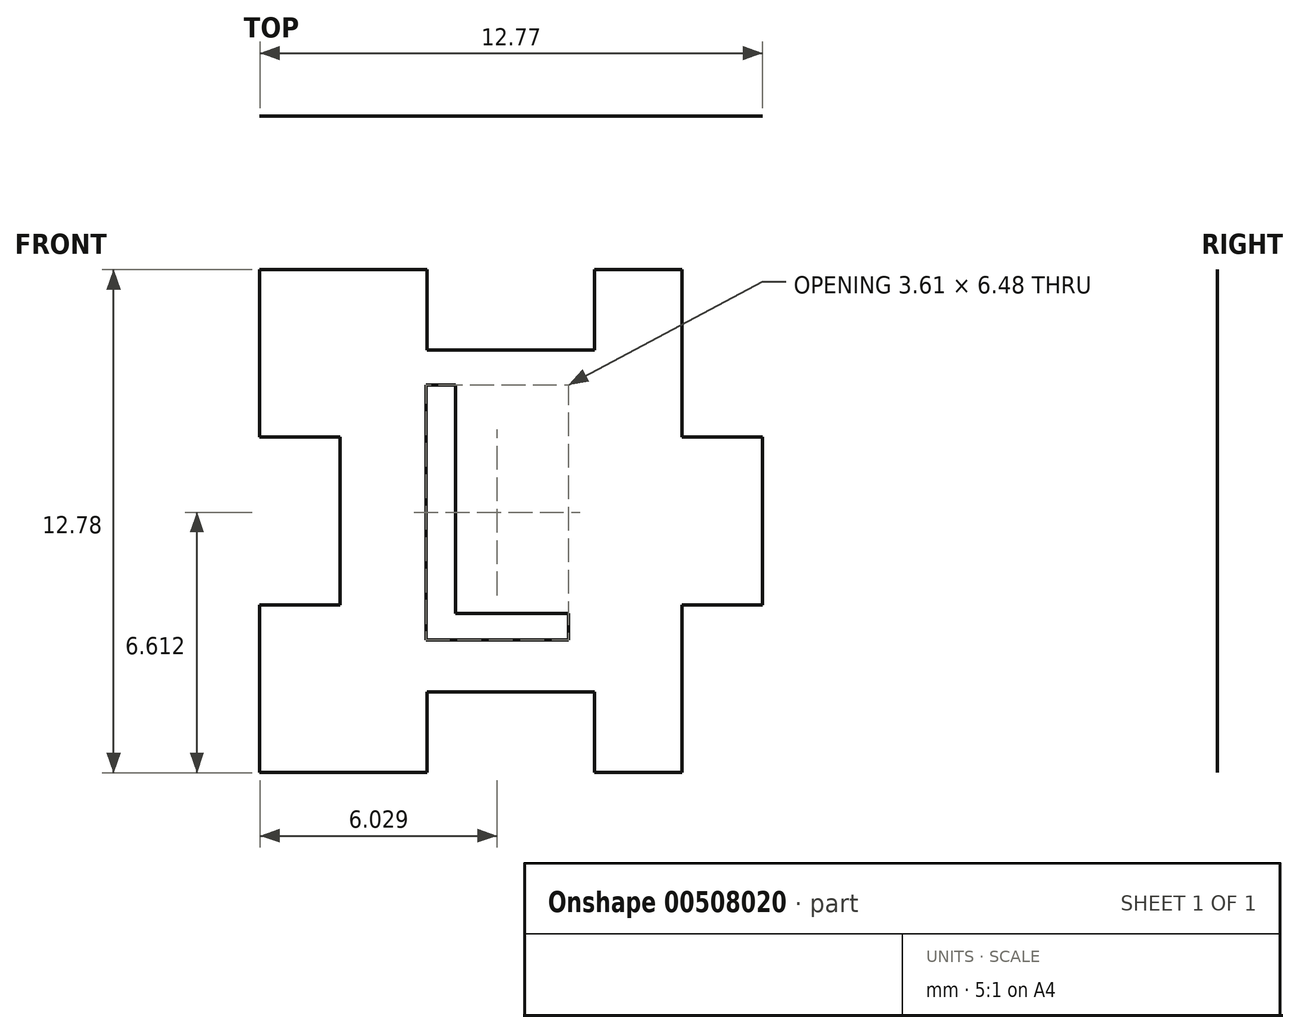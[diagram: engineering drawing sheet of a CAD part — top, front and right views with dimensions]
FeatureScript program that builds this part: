
annotation { "Feature Type Name" : "Feature", "Feature Type Description" : "" }
export const myFeature = defineFeature(function(context is Context, id is Id, definition is map)
    precondition{}
    {
        {
            var Q0;
            Q0=qCreatedBy(makeId("Front.planeOp"),FACE);
            var sketch = newSketch(context, id + "F0", { "sketchPlane" : qUnion([Q0])});
            skLineSegment(sketch, "E0", {"start": v(-10.99, 26.89) * mm, "end": v(-10.99, 29.02) * mm});
            skLineSegment(sketch, "E1", {"start": v(-10.99, 29.02) * mm, "end": v(-13.03, 29.02) * mm});
            skLineSegment(sketch, "E2", {"start": v(-13.03, 29.02) * mm, "end": v(-13.03, 33.28) * mm});
            skLineSegment(sketch, "E3", {"start": v(-13.03, 33.28) * mm, "end": v(-8.78, 33.28) * mm});
            skLineSegment(sketch, "E4", {"start": v(-8.78, 33.28) * mm, "end": v(-8.78, 31.23) * mm});
            skLineSegment(sketch, "E5", {"start": v(-8.78, 31.23) * mm, "end": v(-4.53, 31.23) * mm});
            skLineSegment(sketch, "E6", {"start": v(-4.53, 31.23) * mm, "end": v(-4.53, 33.28) * mm});
            skLineSegment(sketch, "E7", {"start": v(-4.53, 33.28) * mm, "end": v(-2.3, 33.28) * mm});
            skLineSegment(sketch, "E8", {"start": v(-2.3, 33.28) * mm, "end": v(-2.3, 29.02) * mm});
            skLineSegment(sketch, "E9", {"start": v(-2.3, 29.02) * mm, "end": v(-0.26, 29.02) * mm});
            skLineSegment(sketch, "E10", {"start": v(-10.99, 26.89) * mm, "end": v(8.72, 26.89) * mm, "construction": true});
            skLineSegment(sketch, "E11.MirrorCS", {"start": v(-2.3, 24.76) * mm, "end": v(-0.26, 24.76) * mm});
            skLineSegment(sketch, "E12.MirrorCS", {"start": v(-2.3, 20.5) * mm, "end": v(-2.3, 24.76) * mm});
            skLineSegment(sketch, "E13.MirrorCS", {"start": v(-4.53, 20.5) * mm, "end": v(-2.3, 20.5) * mm});
            skLineSegment(sketch, "E14.MirrorCS", {"start": v(-4.53, 22.55) * mm, "end": v(-4.53, 20.5) * mm});
            skLineSegment(sketch, "E15.MirrorCS", {"start": v(-8.78, 22.55) * mm, "end": v(-4.53, 22.55) * mm});
            skLineSegment(sketch, "E16.MirrorCS", {"start": v(-8.78, 20.5) * mm, "end": v(-8.78, 22.55) * mm});
            skLineSegment(sketch, "E17.MirrorCS", {"start": v(-13.03, 20.5) * mm, "end": v(-8.78, 20.5) * mm});
            skLineSegment(sketch, "E18.MirrorCS", {"start": v(-13.03, 24.76) * mm, "end": v(-13.03, 20.5) * mm});
            skLineSegment(sketch, "E19.MirrorCS", {"start": v(-10.99, 24.76) * mm, "end": v(-13.03, 24.76) * mm});
            skLineSegment(sketch, "E20.MirrorCS", {"start": v(-10.99, 26.89) * mm, "end": v(-10.99, 24.76) * mm});
            skLineSegment(sketch, "E21", {"start": v(-0.26, 29.02) * mm, "end": v(-0.26, 24.76) * mm});
            skSolve(sketch);
        }
        {
            var Q0;
            Q0=makeQuery(id+"F0.imprint","IMPRINT",FACE,{"disambiguationData":[TD([[makeQuery(id+"F0.imprint","IMPRINT",EDGE,{"derivedFrom":sQuery(id+"F0.wireOp",EDGE,"E0")}),-1.0]])]});
            extrude(context, id + "F1", {"entities" : qUnion([Q0]), "depth" : .16 / 50.8 * mm, "offsetDistance" : 25 * mm});
        }
        {
            var Q0;
            Q0=makeQuery(id+"F1.opExtrude","CAP_FACE",FACE,{"disambiguationData":[OSD([sQuery(id+"F0.wireOp",EDGE,"E0"),sQuery(id+"F0.wireOp",EDGE,"E1"),sQuery(id+"F0.wireOp",EDGE,"E2"),sQuery(id+"F0.wireOp",EDGE,"E3"),sQuery(id+"F0.wireOp",EDGE,"E4"),sQuery(id+"F0.wireOp",EDGE,"E5"),sQuery(id+"F0.wireOp",EDGE,"E6"),sQuery(id+"F0.wireOp",EDGE,"E7"),sQuery(id+"F0.wireOp",EDGE,"E8"),sQuery(id+"F0.wireOp",EDGE,"E9"),sQuery(id+"F0.wireOp",EDGE,"E11.MirrorCS"),sQuery(id+"F0.wireOp",EDGE,"E12.MirrorCS"),sQuery(id+"F0.wireOp",EDGE,"E13.MirrorCS"),sQuery(id+"F0.wireOp",EDGE,"E14.MirrorCS"),sQuery(id+"F0.wireOp",EDGE,"E15.MirrorCS"),sQuery(id+"F0.wireOp",EDGE,"E16.MirrorCS"),sQuery(id+"F0.wireOp",EDGE,"E17.MirrorCS"),sQuery(id+"F0.wireOp",EDGE,"E18.MirrorCS"),sQuery(id+"F0.wireOp",EDGE,"E19.MirrorCS"),sQuery(id+"F0.wireOp",EDGE,"E20.MirrorCS"),sQuery(id+"F0.wireOp",EDGE,"E21")])],"isStart":false});
            var sketch = newSketch(context, id + "F2", { "sketchPlane" : qUnion([Q0])});
            skText(sketch, "E22", { "text": "L", "fontName": "OpenSans-Regular.ttf"});
            const initialGuessF2  = {"E22": [-0.0097, 0.02387, 1, 0, 0.00654]};
            skSetInitialGuess(sketch, initialGuessF2);
            skSolve(sketch);
        }
        {
            var Q0;
            Q0=makeQuery(id+"F2.imprint","IMPRINT",FACE,{"disambiguationData":[TD([[makeQuery(id+"F2.imprint","IMPRINT",EDGE,{"derivedFrom":sQuery(id+"F2.wireOp",EDGE,"E22.sketch_text.stroke-0")}),-1.0]])]});
            extrude(context, id + "F3", {"entities" : qUnion([Q0]), "operationType" : NewBodyOperationType.REMOVE, "oppositeDirection" : true, "depth" : 1 * mm, "offsetDistance" : 25 * mm});
        }
    });
